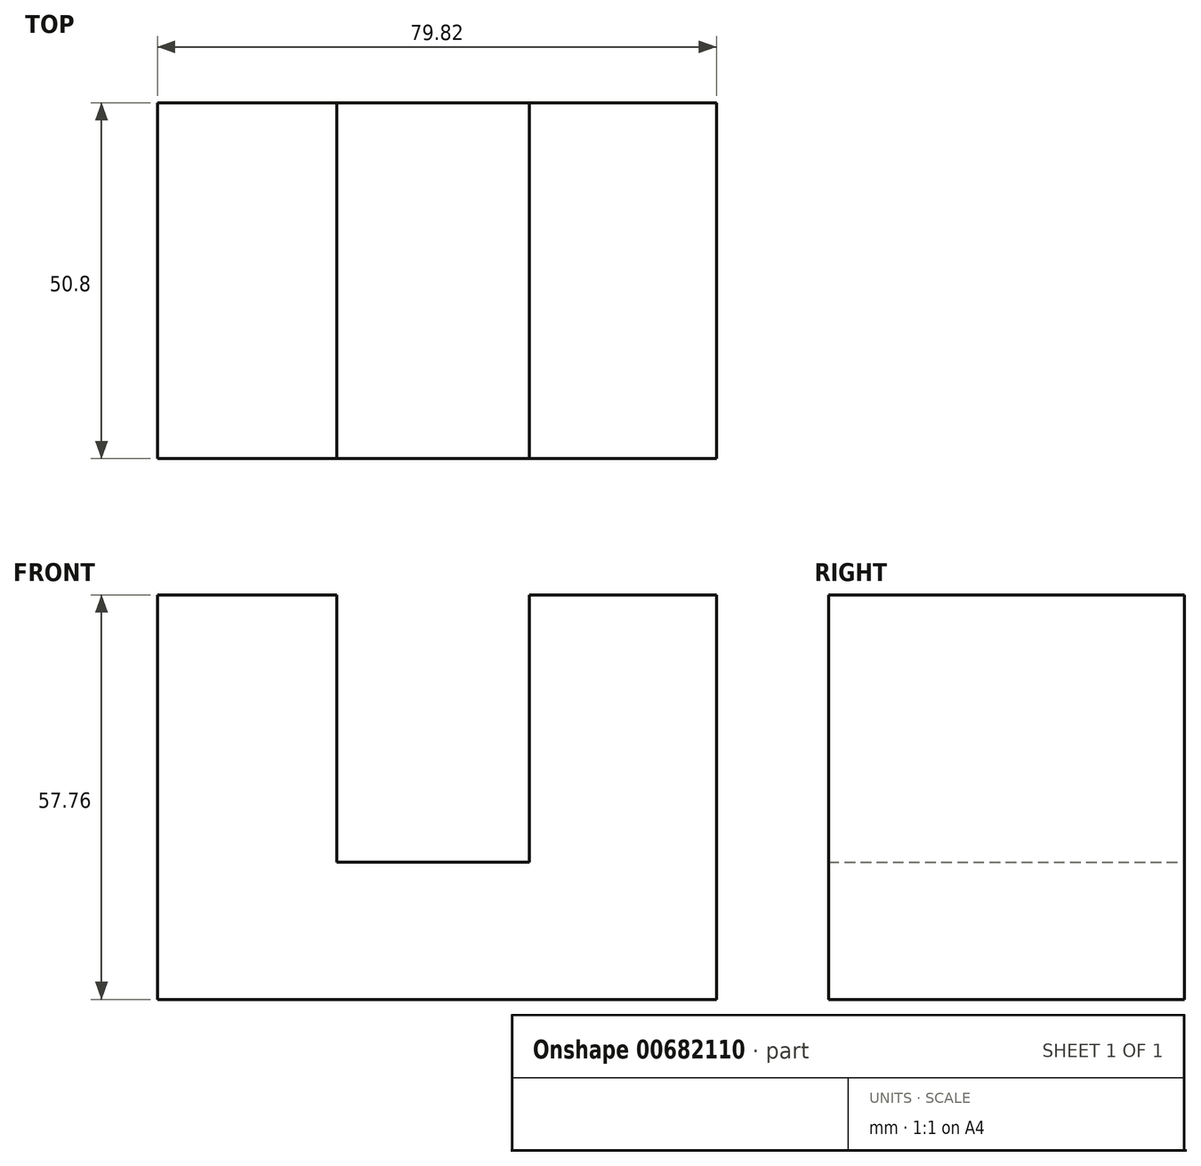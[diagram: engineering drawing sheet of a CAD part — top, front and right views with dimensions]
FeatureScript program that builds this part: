
annotation { "Feature Type Name" : "Feature", "Feature Type Description" : "" }
export const myFeature = defineFeature(function(context is Context, id is Id, definition is map)
    precondition{}
    {
        {
            var Q0;
            Q0=qCreatedBy(makeId("Front.planeOp"),FACE);
            var sketch = newSketch(context, id + "F0", { "sketchPlane" : qUnion([Q0])});
            skLineSegment(sketch, "E0", {"start": v(24.16, 0) * mm, "end": v(24.16, 57.76) * mm});
            skLineSegment(sketch, "E1", {"start": v(24.16, 57.76) * mm, "end": v(-2.58, 57.76) * mm});
            skLineSegment(sketch, "E2", {"start": v(-2.58, 57.76) * mm, "end": v(-2.58, 19.57) * mm});
            skLineSegment(sketch, "E3", {"start": v(-2.58, 19.57) * mm, "end": v(-30.08, 19.57) * mm});
            skLineSegment(sketch, "E4", {"start": v(-30.08, 19.57) * mm, "end": v(-30.08, 57.76) * mm});
            skPoint(sketch, "E5.start.orphan", {"position": v(-64.07, 0) * mm});
            skLineSegment(sketch, "E6", {"start": v(-30.08, 57.76) * mm, "end": v(-55.66, 57.76) * mm});
            skLineSegment(sketch, "E7", {"start": v(-55.66, 57.76) * mm, "end": v(-55.66, 0) * mm});
            skLineSegment(sketch, "E8", {"start": v(-55.66, 0) * mm, "end": v(24.16, 0) * mm});
            skSolve(sketch);
        }
        {
            var Q0;
            Q0 = qSketchRegion(id + "F0", true);
            extrude(context, id + "F1", {"entities" : qUnion([Q0]), "depth" : 50.8 * mm, "offsetDistance" : 25.4 * mm});
        }
    });
